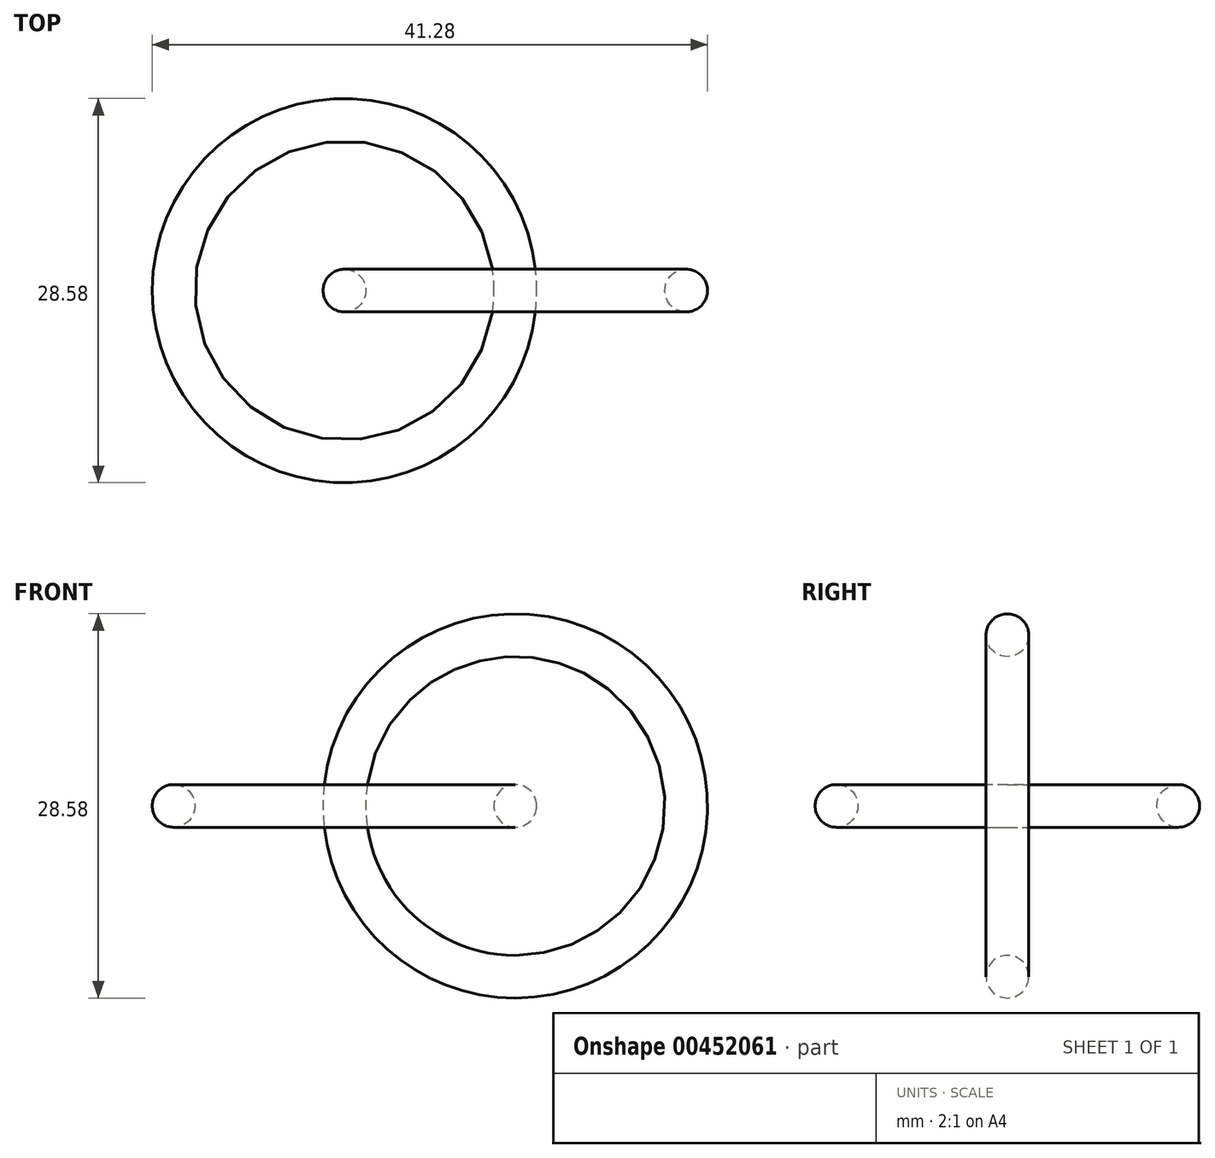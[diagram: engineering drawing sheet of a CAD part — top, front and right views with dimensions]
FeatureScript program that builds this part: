
annotation { "Feature Type Name" : "Feature", "Feature Type Description" : "" }
export const myFeature = defineFeature(function(context is Context, id is Id, definition is map)
    precondition{}
    {
        {
            var Q0;
            Q0=qCreatedBy(makeId("Top.planeOp"),FACE);
            var sketch = newSketch(context, id + "F0", { "sketchPlane" : qUnion([Q0])});
            skCircle(sketch, "E0", {"center": v(0, 0) * mm, "radius": 12.7 * mm});
            skSolve(sketch);
        }
        {
            var Q0;
            Q0=qCreatedBy(makeId("Top.planeOp"),FACE);
            var sketch = newSketch(context, id + "F1", { "sketchPlane" : qUnion([Q0])});
            skCircle(sketch, "E1", {"center": v(0, 0) * mm, "radius": 1.59 * mm});
            skSolve(sketch);
        }
        {
            var Q0;
            Q0=qCreatedBy(makeId("Front.planeOp"),FACE);
            var sketch = newSketch(context, id + "F2", { "sketchPlane" : qUnion([Q0])});
            skLineSegment(sketch, "E2.0", {"start": v(-12.7, 0) * mm, "end": v(12.7, 0) * mm});
            skCircle(sketch, "E3", {"center": v(12.7, 0) * mm, "radius": 12.7 * mm});
            skSolve(sketch);
        }
        {
            var Q0;
            Q0=qCreatedBy(makeId("Front.planeOp"),FACE);
            var sketch = newSketch(context, id + "F3", { "sketchPlane" : qUnion([Q0])});
            skCircle(sketch, "E4.0", {"center": v(12.7, 0) * mm, "radius": 12.7 * mm});
            skCircle(sketch, "E5", {"center": v(12.7, 0) * mm, "radius": 1.59 * mm});
            skSolve(sketch);
        }
        {
            var Q0;
            Q0 = qSketchRegion(id + "F1", true);
            var Q1;
            Q1=sQuery(id+"F3.wireOp",EDGE,"E4.0");
            sweep(context, id + "F4", {"profiles" : qUnion([Q0]), "path" : qUnion([Q1])});
        }
        {
            var Q0;
            Q0=makeQuery(id+"F3.imprint","IMPRINT",FACE,{"disambiguationData":[TD([[makeQuery(id+"F3.imprint","IMPRINT",EDGE,{"derivedFrom":sQuery(id+"F3.wireOp",EDGE,"E5")}),1.0]])]});
            var Q1;
            Q1=sQuery(id+"F0.wireOp",EDGE,"E0");
            sweep(context, id + "F5", {"profiles" : qUnion([Q0]), "path" : qUnion([Q1])});
        }
    });
